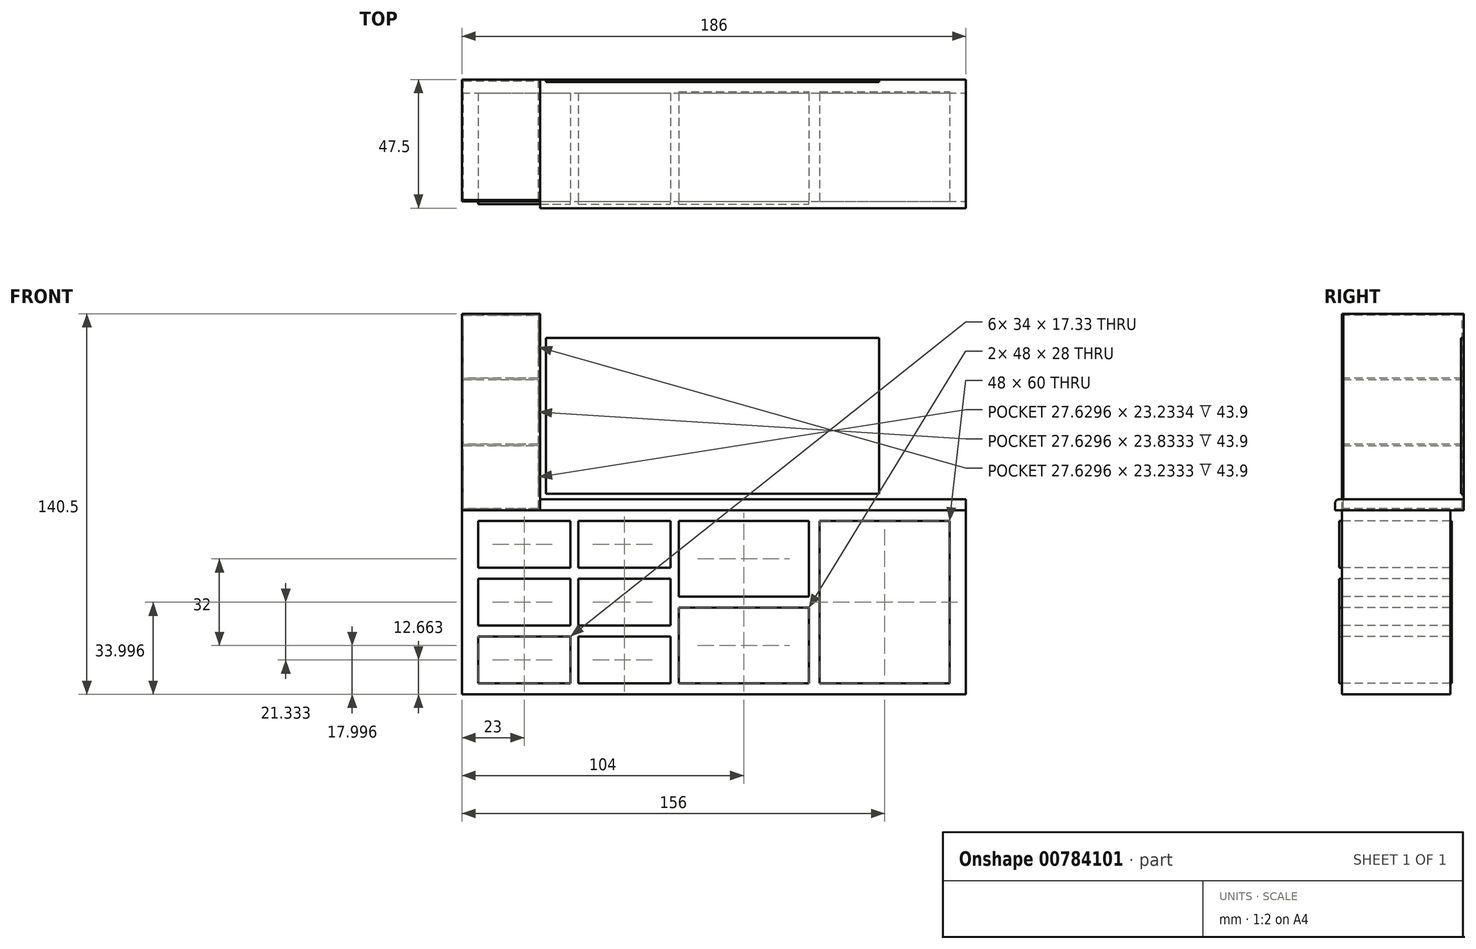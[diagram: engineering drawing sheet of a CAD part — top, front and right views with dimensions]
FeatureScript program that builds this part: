
annotation { "Feature Type Name" : "Feature", "Feature Type Description" : "" }
export const myFeature = defineFeature(function(context is Context, id is Id, definition is map)
    precondition{}
    {
        {
            var Q0;
            Q0=qCreatedBy(makeId("Front.planeOp"),FACE);
            var sketch = newSketch(context, id + "F0", { "sketchPlane" : qUnion([Q0])});
            skLineSegment(sketch, "E0.bottom", {"start": v(-92.5, -84.8) * mm, "end": v(93.5, -84.8) * mm});
            skLineSegment(sketch, "E0.left", {"start": v(-92.5, -84.8) * mm, "end": v(-92.5, -12.4) * mm});
            skLineSegment(sketch, "E0.right", {"start": v(93.5, -84.8) * mm, "end": v(93.5, -16.8) * mm});
            skLineSegment(sketch, "E1.bottom", {"start": v(93.5, -16.8) * mm, "end": v(-63.67, -16.8) * mm});
            skLineSegment(sketch, "E1.top", {"start": v(93.5, -12.8) * mm, "end": v(-63.67, -12.8) * mm});
            skLineSegment(sketch, "E1.left", {"start": v(93.5, -16.8) * mm, "end": v(93.5, -12.8) * mm});
            skLineSegment(sketch, "E1.right", {"start": v(-63.67, -16.8) * mm, "end": v(-63.67, -12.8) * mm});
            skLineSegment(sketch, "E2.top", {"start": v(-92.5, 55.7) * mm, "end": v(-63.67, 55.7) * mm});
            skLineSegment(sketch, "E2.left", {"start": v(-92.5, -12.4) * mm, "end": v(-92.5, 55.7) * mm});
            skLineSegment(sketch, "E2.right", {"start": v(-63.67, -14.83) * mm, "end": v(-63.67, 55.7) * mm});
            skPoint(sketch, "E3.oppositeSnap0", {"position": v(-92.5, -48.6) * mm});
            skLineSegment(sketch, "E3.bottom", {"start": v(-86.5, -20.8) * mm, "end": v(-52.5, -20.8) * mm});
            skLineSegment(sketch, "E3.right", {"start": v(-52.5, -20.8) * mm, "end": v(-52.5, -38.14) * mm});
            skLineSegment(sketch, "E4.bottom", {"start": v(-12.5, -20.8) * mm, "end": v(35.5, -20.8) * mm});
            skLineSegment(sketch, "E4.top", {"start": v(-12.5, -48.8) * mm, "end": v(35.5, -48.8) * mm});
            skLineSegment(sketch, "E4.left", {"start": v(-12.5, -20.8) * mm, "end": v(-12.5, -48.8) * mm});
            skLineSegment(sketch, "E4.right", {"start": v(35.5, -20.8) * mm, "end": v(35.5, -48.8) * mm});
            skLineSegment(sketch, "E5.bottom", {"start": v(-12.5, -52.8) * mm, "end": v(35.5, -52.8) * mm});
            skLineSegment(sketch, "E5.top", {"start": v(-12.5, -80.8) * mm, "end": v(35.5, -80.8) * mm});
            skLineSegment(sketch, "E5.left", {"start": v(-12.5, -52.8) * mm, "end": v(-12.5, -80.8) * mm});
            skLineSegment(sketch, "E5.right", {"start": v(35.5, -52.8) * mm, "end": v(35.5, -80.8) * mm});
            skLineSegment(sketch, "E6.bottom", {"start": v(39.5, -80.8) * mm, "end": v(87.5, -80.8) * mm});
            skLineSegment(sketch, "E6.top", {"start": v(39.5, -20.8) * mm, "end": v(87.5, -20.8) * mm});
            skLineSegment(sketch, "E6.left", {"start": v(39.5, -80.8) * mm, "end": v(39.5, -20.8) * mm});
            skLineSegment(sketch, "E6.right", {"start": v(87.5, -80.8) * mm, "end": v(87.5, -20.8) * mm});
            skLineSegment(sketch, "E7.bottom", {"start": v(61.5, -10.75) * mm, "end": v(-61.5, -10.75) * mm});
            skLineSegment(sketch, "E7.top", {"start": v(61.5, 46.75) * mm, "end": v(-61.5, 46.75) * mm});
            skLineSegment(sketch, "E7.left", {"start": v(61.5, -10.75) * mm, "end": v(61.5, 46.75) * mm});
            skLineSegment(sketch, "E7.right", {"start": v(-61.5, -10.75) * mm, "end": v(-61.5, 46.75) * mm});
            skPoint(sketch, "E7.middle", {"position": v(0, 18) * mm});
            skLineSegment(sketch, "E8", {"start": v(-86.5, -20.8) * mm, "end": v(-86.5, -38.14) * mm});
            skLineSegment(sketch, "E9", {"start": v(-86.5, -38.14) * mm, "end": v(-52.5, -38.14) * mm});
            skLineSegment(sketch, "E10.bottom", {"start": v(-86.5, -42.14) * mm, "end": v(-52.5, -42.14) * mm});
            skLineSegment(sketch, "E10.top", {"start": v(-86.5, -59.47) * mm, "end": v(-52.5, -59.47) * mm});
            skLineSegment(sketch, "E10.left", {"start": v(-86.5, -42.14) * mm, "end": v(-86.5, -59.47) * mm});
            skLineSegment(sketch, "E10.right", {"start": v(-52.5, -42.14) * mm, "end": v(-52.5, -59.47) * mm});
            skLineSegment(sketch, "E11.bottom", {"start": v(-86.5, -63.47) * mm, "end": v(-52.5, -63.47) * mm});
            skLineSegment(sketch, "E11.top", {"start": v(-86.5, -80.8) * mm, "end": v(-52.5, -80.8) * mm});
            skLineSegment(sketch, "E11.left", {"start": v(-86.5, -63.47) * mm, "end": v(-86.5, -80.8) * mm});
            skLineSegment(sketch, "E11.right", {"start": v(-52.5, -63.47) * mm, "end": v(-52.5, -80.8) * mm});
            skLineSegment(sketch, "E12.bottom", {"start": v(-49.5, -20.8) * mm, "end": v(-15.5, -20.8) * mm});
            skLineSegment(sketch, "E12.top", {"start": v(-49.5, -38.14) * mm, "end": v(-15.5, -38.14) * mm});
            skLineSegment(sketch, "E12.left", {"start": v(-49.5, -20.8) * mm, "end": v(-49.5, -38.14) * mm});
            skLineSegment(sketch, "E12.right", {"start": v(-15.5, -20.8) * mm, "end": v(-15.5, -38.14) * mm});
            skLineSegment(sketch, "E13.bottom", {"start": v(-49.5, -42.14) * mm, "end": v(-15.5, -42.14) * mm});
            skLineSegment(sketch, "E13.top", {"start": v(-49.5, -59.47) * mm, "end": v(-15.5, -59.47) * mm});
            skLineSegment(sketch, "E13.left", {"start": v(-49.5, -42.14) * mm, "end": v(-49.5, -59.47) * mm});
            skLineSegment(sketch, "E13.right", {"start": v(-15.5, -42.14) * mm, "end": v(-15.5, -59.47) * mm});
            skLineSegment(sketch, "E14.bottom", {"start": v(-49.5, -63.47) * mm, "end": v(-15.5, -63.47) * mm});
            skLineSegment(sketch, "E14.top", {"start": v(-49.5, -80.8) * mm, "end": v(-15.5, -80.8) * mm});
            skLineSegment(sketch, "E14.left", {"start": v(-49.5, -63.47) * mm, "end": v(-49.5, -80.8) * mm});
            skLineSegment(sketch, "E14.right", {"start": v(-15.5, -63.47) * mm, "end": v(-15.5, -80.8) * mm});
            skLineSegment(sketch, "E15", {"start": v(-63.67, -16.8) * mm, "end": v(-92.5, -16.8) * mm});
            skSolve(sketch);
        }
        {
            var Q0;
            {var subQ1=sQuery(id+"F0.wireOp",EDGE,"E0.bottom");Q0=makeQuery(id+"F0.imprint","IMPRINT",FACE,{"disambiguationData":[TD([[makeQuery(id+"F0.imprint","IMPRINT",EDGE,{"derivedFrom":subQ1}),1.0]])]});}
            extrude(context, id + "F1", {"entities" : qUnion([Q0]), "oppositeDirection" : true, "depth" : 40 * mm, "offsetDistance" : 25 * mm});
        }
        {
            var Q0;
            {var subQ3=sQuery(id+"F0.wireOp",EDGE,"E1.right");Q0=makeQuery(id+"F0.imprint","IMPRINT",FACE,{"disambiguationData":[TD([[makeQuery(id+"F0.imprint","IMPRINT",EDGE,{"derivedFrom":subQ3}),1.0]])]});}
            extrude(context, id + "F2", {"entities" : qUnion([Q0]), "oppositeDirection" : true, "depth" : 45 * mm, "offsetDistance" : 25 * mm, "hasSecondDirection" : true, "secondDirectionOppositeDirection" : true, "secondDirectionDepth" : 0.5 * mm});
        }
        {
            var Q0;
            Q0=makeQuery(id+"F0.imprint","IMPRINT",FACE,{"disambiguationData":[TD([[makeQuery(id+"F0.imprint","IMPRINT",EDGE,{"derivedFrom":sQuery(id+"F0.wireOp",EDGE,"E1.bottom")}),-1.0]])]});
            var Q1;
            Q1=makeQuery(id+"F2.opExtrude","CAP_VERTEX",VERTEX,{"disambiguationData":[OSD([sQuery(id+"F0.wireOp",EDGE,"E1.bottom"),sQuery(id+"F0.wireOp",EDGE,"E1.right"),sQuery(id+"F0.wireOp",EDGE,"E15")])],"isStart":false});
            extrude(context, id + "F3", {"entities" : qUnion([Q0]), "oppositeDirection" : true, "depth" : 45 * mm, "endBoundEntityVertex" : qUnion([Q1]), "offsetDistance" : 2 * mm, "hasSecondDirection" : true, "secondDirectionOppositeDirection" : false, "secondDirectionDepth" : 2.5 * mm});
        }
        {
            var Q0;
            Q0=makeQuery(id+"F0.imprint","IMPRINT",FACE,{"disambiguationData":[TD([[makeQuery(id+"F0.imprint","IMPRINT",EDGE,{"derivedFrom":sQuery(id+"F0.wireOp",EDGE,"E7.bottom")}),-1.0]])]});
            var Q1;
            Q1=sQuery(id+"F0.wireOp",EDGE,"E7.top");
            var Q2;
            Q2=sQuery(id+"F0.wireOp",EDGE,"E7.left");
            var Q3;
            Q3=sQuery(id+"F0.wireOp",EDGE,"E7.bottom");
            var Q4;
            Q4=sQuery(id+"F0.wireOp",EDGE,"E7.right");
            var Q5;
            Q5=makeQuery(id+"F3.opExtrude","CAP_FACE",FACE,{"disambiguationData":[OSD([sQuery(id+"F0.wireOp",EDGE,"E1.bottom"),sQuery(id+"F0.wireOp",EDGE,"E1.top"),sQuery(id+"F0.wireOp",EDGE,"E1.left"),sQuery(id+"F0.wireOp",EDGE,"E1.right"),sQuery(id+"F0.wireOp",EDGE,"E2.right")])],"isStart":false});
            extrude(context, id + "F4", {"entities" : qUnion([Q0]), "surfaceEntities" : qUnion([Q1, Q2, Q3, Q4]), "oppositeDirection" : true, "depth" : 45 * mm, "endBoundEntityFace" : qUnion([Q5]), "offsetDistance" : 45 * mm, "offsetOppositeDirection" : true, "hasSecondDirection" : true, "secondDirectionOppositeDirection" : true, "secondDirectionDepth" : 44 * mm});
        }
        {
            var Q0;
            Q0=makeQuery(id+"F2.opExtrude","CAP_FACE",FACE,{"disambiguationData":[OSD([sQuery(id+"F0.wireOp",EDGE,"E0.left"),sQuery(id+"F0.wireOp",EDGE,"E1.right"),sQuery(id+"F0.wireOp",EDGE,"E2.top"),sQuery(id+"F0.wireOp",EDGE,"E2.left"),sQuery(id+"F0.wireOp",EDGE,"E2.right"),sQuery(id+"F0.wireOp",EDGE,"E15")])],"isStart":true});
            shell(context, id + "F5", {"entities" : qUnion([Q0]), "thickness" : 0.6 * mm});
        }
        {
            var Q0;
            Q0=makeQuery(id+"F2.opExtrude","SWEPT_FACE",FACE,{"disambiguationData":[OSD([sQuery(id+"F0.wireOp",EDGE,"E0.left"),sQuery(id+"F0.wireOp",EDGE,"E2.left")])]});
            var sketch = newSketch(context, id + "F6", { "sketchPlane" : qUnion([Q0])});
            skLineSegment(sketch, "E16", {"start": v(-0.5, 31.86) * mm, "end": v(-45, 31.86) * mm});
            skLineSegment(sketch, "E17", {"start": v(-0.5, 7.53) * mm, "end": v(-45, 7.53) * mm});
            skLineSegment(sketch, "E18", {"start": v(-45, 31.86) * mm, "end": v(-45, 31.36) * mm});
            skLineSegment(sketch, "E19", {"start": v(-45, 31.36) * mm, "end": v(-0.5, 31.36) * mm});
            skLineSegment(sketch, "E20", {"start": v(-0.5, 31.36) * mm, "end": v(-0.5, 31.86) * mm});
            skLineSegment(sketch, "E21", {"start": v(-45, 7.53) * mm, "end": v(-45, 7.03) * mm});
            skLineSegment(sketch, "E22", {"start": v(-45, 7.03) * mm, "end": v(-0.5, 7.03) * mm});
            skLineSegment(sketch, "E23", {"start": v(-0.5, 7.03) * mm, "end": v(-0.5, 7.53) * mm});
            skLineSegment(sketch, "E24", {"start": v(-45, -16.8) * mm, "end": v(-45, 7.03) * mm});
            skLineSegment(sketch, "E25", {"start": v(-45, 7.53) * mm, "end": v(-45, 31.36) * mm});
            skLineSegment(sketch, "E26", {"start": v(-45, 31.86) * mm, "end": v(-45, 55.7) * mm});
            skSolve(sketch);
        }
        {
            var Q0;
            Q0 = qSketchRegion(id + "F6", true);
            var Q1;
            Q1=makeQuery(id+"F2.opExtrude","SWEPT_BODY",BODY,{"disambiguationData":[OSD([sQuery(id+"F0.wireOp",EDGE,"E0.left"),sQuery(id+"F0.wireOp",EDGE,"E1.right"),sQuery(id+"F0.wireOp",EDGE,"E2.top"),sQuery(id+"F0.wireOp",EDGE,"E2.left"),sQuery(id+"F0.wireOp",EDGE,"E2.right"),sQuery(id+"F0.wireOp",EDGE,"E15")])]});
            extrude(context, id + "F7", {"entities" : qUnion([Q0]), "operationType" : NewBodyOperationType.ADD, "endBound" : BoundingType.UP_TO_BODY, "oppositeDirection" : true, "depth" : 25 * mm, "endBoundEntityBody" : qUnion([Q1]), "offsetDistance" : 25 * mm});
        }
        {
            var Q0;
            Q0=makeQuery(id+"F3.opExtrude","CAP_EDGE",EDGE,{"disambiguationData":[OSD([sQuery(id+"F0.wireOp",EDGE,"E1.top")])],"isStart":true});
            fillet(context, id + "F8", {"entities" : qUnion([Q0]), "radius" : 1.5 * mm, "tangentPropagation" : true, "allowEdgeOverflow" : false});
        }
        {
            var Q0;
            Q0=makeQuery(id+"F0.imprint","IMPRINT",FACE,{"disambiguationData":[TD([[makeQuery(id+"F0.imprint","IMPRINT",EDGE,{"derivedFrom":sQuery(id+"F0.wireOp",EDGE,"E3.bottom")}),-1.0]])]});
            var Q1;
            Q1=makeQuery(id+"F0.imprint","IMPRINT",FACE,{"disambiguationData":[TD([[makeQuery(id+"F0.imprint","IMPRINT",EDGE,{"derivedFrom":sQuery(id+"F0.wireOp",EDGE,"E12.bottom")}),-1.0]])]});
            var Q2;
            Q2=makeQuery(id+"F0.imprint","IMPRINT",FACE,{"disambiguationData":[TD([[makeQuery(id+"F0.imprint","IMPRINT",EDGE,{"derivedFrom":sQuery(id+"F0.wireOp",EDGE,"E13.bottom")}),-1.0]])]});
            var Q3;
            Q3=makeQuery(id+"F0.imprint","IMPRINT",FACE,{"disambiguationData":[TD([[makeQuery(id+"F0.imprint","IMPRINT",EDGE,{"derivedFrom":sQuery(id+"F0.wireOp",EDGE,"E10.bottom")}),-1.0]])]});
            var Q4;
            Q4=makeQuery(id+"F0.imprint","IMPRINT",FACE,{"disambiguationData":[TD([[makeQuery(id+"F0.imprint","IMPRINT",EDGE,{"derivedFrom":sQuery(id+"F0.wireOp",EDGE,"E11.bottom")}),-1.0]])]});
            var Q5;
            Q5=makeQuery(id+"F0.imprint","IMPRINT",FACE,{"disambiguationData":[TD([[makeQuery(id+"F0.imprint","IMPRINT",EDGE,{"derivedFrom":sQuery(id+"F0.wireOp",EDGE,"E14.bottom")}),-1.0]])]});
            var Q6;
            Q6=makeQuery(id+"F0.imprint","IMPRINT",FACE,{"disambiguationData":[TD([[makeQuery(id+"F0.imprint","IMPRINT",EDGE,{"derivedFrom":sQuery(id+"F0.wireOp",EDGE,"E5.bottom")}),-1.0]])]});
            extrude(context, id + "F9", {"entities" : qUnion([Q0, Q1, Q2, Q3, Q4, Q5, Q6]), "depth" : 1 * mm, "offsetDistance" : 25 * mm});
        }
        {
            var Q0;
            Q0=makeQuery(id+"F0.imprint","IMPRINT",FACE,{"disambiguationData":[TD([[makeQuery(id+"F0.imprint","IMPRINT",EDGE,{"derivedFrom":sQuery(id+"F0.wireOp",EDGE,"E4.bottom")}),-1.0]])]});
            var Q1;
            Q1=makeQuery(id+"F0.imprint","IMPRINT",FACE,{"disambiguationData":[TD([[makeQuery(id+"F0.imprint","IMPRINT",EDGE,{"derivedFrom":sQuery(id+"F0.wireOp",EDGE,"E6.bottom")}),1.0]])]});
            extrude(context, id + "F10", {"entities" : qUnion([Q0, Q1]), "operationType" : NewBodyOperationType.ADD, "oppositeDirection" : true, "depth" : 40.5 * mm, "offsetDistance" : 25 * mm, "hasSecondDirection" : true, "secondDirectionOppositeDirection" : true, "secondDirectionDepth" : 40 * mm});
        }
        {
            var Q0;
            {var subQ3=sQuery(id+"F0.wireOp",EDGE,"E1.right");Q0=makeQuery(id+"F0.imprint","IMPRINT",FACE,{"disambiguationData":[TD([[makeQuery(id+"F0.imprint","IMPRINT",EDGE,{"derivedFrom":subQ3}),1.0]])]});}
            extrude(context, id + "F11", {"entities" : qUnion([Q0]), "depth" : 0 * mm, "offsetDistance" : 25 * mm, "hasSecondDirection" : true, "secondDirectionOppositeDirection" : true, "secondDirectionDepth" : 0.5 * mm});
        }
    });
